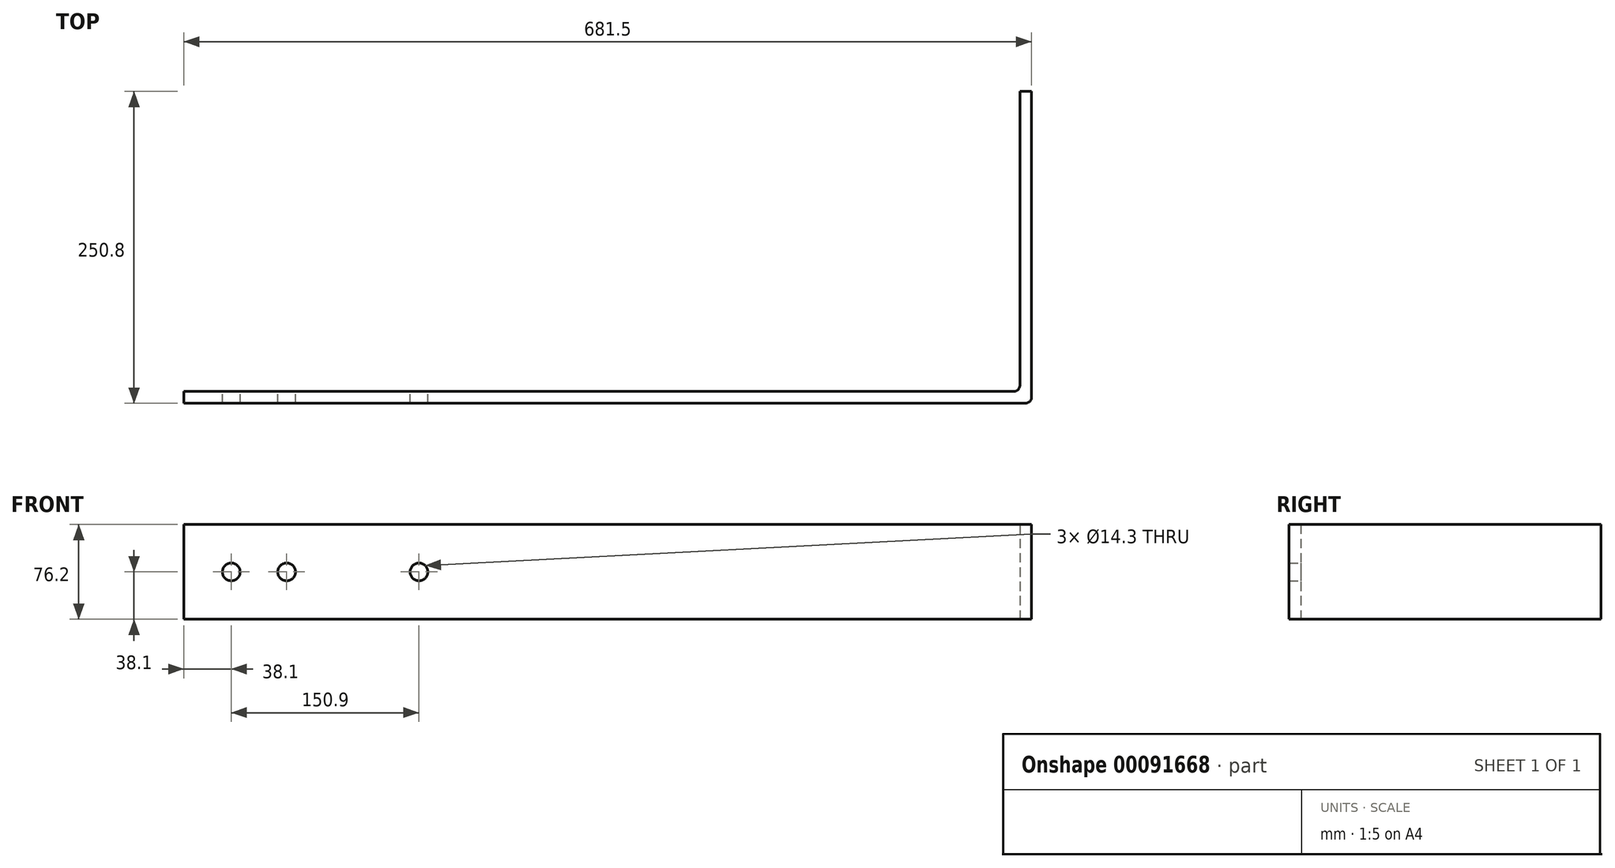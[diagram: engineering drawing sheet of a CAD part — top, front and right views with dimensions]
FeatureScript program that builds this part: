
annotation { "Feature Type Name" : "Feature", "Feature Type Description" : "" }
export const myFeature = defineFeature(function(context is Context, id is Id, definition is map)
    precondition{}
    {
        {
            var Q0;
            Q0=qCreatedBy(makeId("Top.planeOp"),FACE);
            var sketch = newSketch(context, id + "F0", { "sketchPlane" : qUnion([Q0])});
            skLineSegment(sketch, "E0", {"start": v(0, 0) * mm, "end": v(681.5, 0) * mm});
            skLineSegment(sketch, "E1", {"start": v(681.5, 0) * mm, "end": v(681.5, 250.8) * mm});
            skLineSegment(sketch, "E2", {"start": v(681.5, 250.8) * mm, "end": v(672, 250.8) * mm});
            skLineSegment(sketch, "E3", {"start": v(672, 250.8) * mm, "end": v(672, 9.5) * mm});
            skLineSegment(sketch, "E4", {"start": v(672, 9.5) * mm, "end": v(0, 9.5) * mm});
            skLineSegment(sketch, "E5", {"start": v(0, 9.5) * mm, "end": v(0, 0) * mm});
            skSolve(sketch);
        }
        {
            var Q0;
            Q0=makeQuery(id+"F0.imprint","IMPRINT",FACE,{"disambiguationData":[TD([[makeQuery(id+"F0.imprint","IMPRINT",EDGE,{"derivedFrom":sQuery(id+"F0.wireOp",EDGE,"E0")}),1.0]])]});
            extrude(context, id + "F1", {"entities" : qUnion([Q0]), "depth" : 76.2 * mm});
        }
        {
            var Q0;
            Q0=makeQuery(id+"F1.opExtrude","SWEPT_FACE",FACE,{"disambiguationData":[OSD([sQuery(id+"F0.wireOp",EDGE,"E4")])]});
            var sketch = newSketch(context, id + "F2", { "sketchPlane" : qUnion([Q0])});
            skCircle(sketch, "E6", {"center": v(-38.1, 38.1) * mm, "radius": 7.15 * mm});
            skPoint(sketch, "E6.centerSnap0", {"position": v(0, 38.1) * mm});
            skCircle(sketch, "E7", {"center": v(-82.6, 38.1) * mm, "radius": 7.15 * mm});
            skCircle(sketch, "E8", {"center": v(-189, 38.1) * mm, "radius": 7.15 * mm});
            skSolve(sketch);
        }
        {
            var Q0;
            Q0=makeQuery(id+"F2.imprint","IMPRINT",FACE,{"disambiguationData":[TD([[makeQuery(id+"F2.imprint","IMPRINT",EDGE,{"derivedFrom":sQuery(id+"F2.wireOp",EDGE,"E6")}),1.0]])]});
            var Q1;
            Q1=makeQuery(id+"F2.imprint","IMPRINT",FACE,{"disambiguationData":[TD([[makeQuery(id+"F2.imprint","IMPRINT",EDGE,{"derivedFrom":sQuery(id+"F2.wireOp",EDGE,"E7")}),1.0]])]});
            var Q2;
            Q2=makeQuery(id+"F2.imprint","IMPRINT",FACE,{"disambiguationData":[TD([[makeQuery(id+"F2.imprint","IMPRINT",EDGE,{"derivedFrom":sQuery(id+"F2.wireOp",EDGE,"E8")}),1.0]])]});
            extrude(context, id + "F3", {"entities" : qUnion([Q0, Q1, Q2]), "operationType" : NewBodyOperationType.REMOVE, "endBound" : BoundingType.THROUGH_ALL, "oppositeDirection" : true, "depth" : 25 * mm});
        }
        {
            var Q0;
            Q0=makeQuery(id+"F1.opExtrude","SWEPT_EDGE",EDGE,{"disambiguationData":[OSD([sQuery(id+"F0.wireOp",EDGE,"E0"),sQuery(id+"F0.wireOp",EDGE,"E1")])]});
            fillet(context, id + "F4", {"entities" : qUnion([Q0]), "radius" : 5 * mm, "tangentPropagation" : true, "allowEdgeOverflow" : false});
        }
        {
            var Q0;
            Q0=makeQuery(id+"F1.opExtrude","SWEPT_EDGE",EDGE,{"disambiguationData":[OSD([sQuery(id+"F0.wireOp",EDGE,"E3"),sQuery(id+"F0.wireOp",EDGE,"E4")])]});
            fillet(context, id + "F5", {"entities" : qUnion([Q0]), "radius" : 5 * mm, "tangentPropagation" : true, "allowEdgeOverflow" : false});
        }
    });
